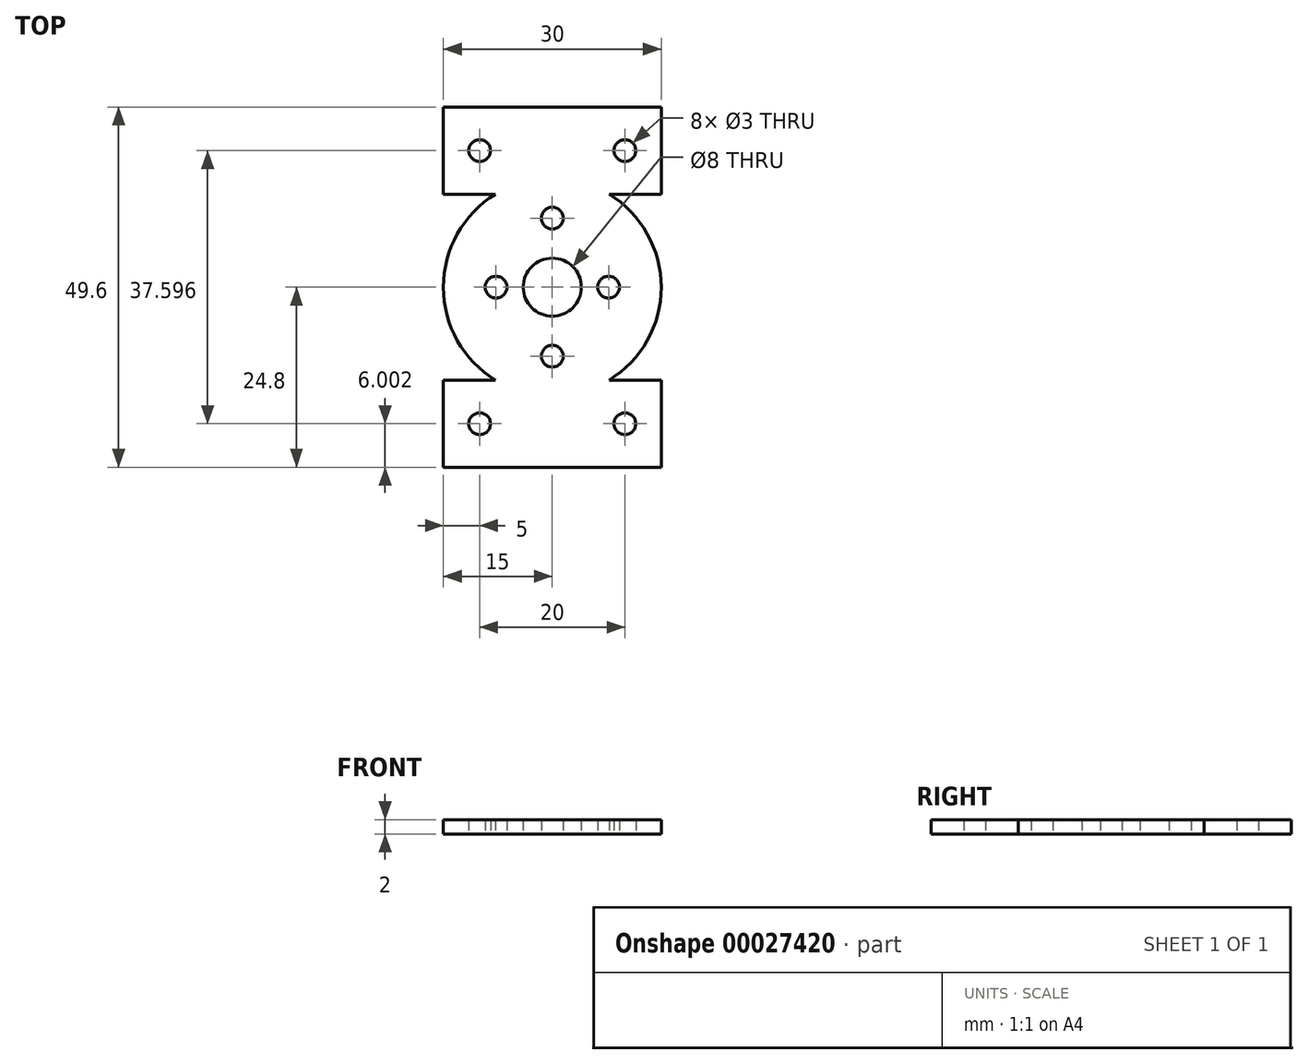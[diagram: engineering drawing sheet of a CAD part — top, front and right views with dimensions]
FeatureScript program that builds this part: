
annotation { "Feature Type Name" : "Feature", "Feature Type Description" : "" }
export const myFeature = defineFeature(function(context is Context, id is Id, definition is map)
    precondition{}
    {
        {
            var Q0;
            Q0=qCreatedBy(makeId("Top.planeOp"),FACE);
            var sketch = newSketch(context, id + "F0", { "sketchPlane" : qUnion([Q0])});
            skCircle(sketch, "E0", {"center": v(0, 9.5) * mm, "radius": 1.5 * mm});
            skCircle(sketch, "E1", {"center": v(-7.75, 0) * mm, "radius": 1.5 * mm});
            skCircle(sketch, "E2", {"center": v(0, 0) * mm, "radius": 4 * mm});
            skCircle(sketch, "E3", {"center": v(0, 0) * mm, "radius": 15 * mm});
            skLineSegment(sketch, "E4.rect.bottom", {"start": v(15, 12.8) * mm, "end": v(7.82, 12.8) * mm});
            skLineSegment(sketch, "E4.rect.top", {"start": v(15, 24.8) * mm, "end": v(-15, 24.8) * mm});
            skLineSegment(sketch, "E4.rect.left", {"start": v(15, 12.8) * mm, "end": v(15, 24.8) * mm});
            skLineSegment(sketch, "E4.rect.right", {"start": v(-15, 12.8) * mm, "end": v(-15, 24.8) * mm});
            skPoint(sketch, "E4.rect.middle", {"position": v(0, 18.8) * mm});
            skLineSegment(sketch, "E5.MirrorCS", {"start": v(15, -12.8) * mm, "end": v(7.82, -12.8) * mm});
            skLineSegment(sketch, "E6.MirrorCS", {"start": v(15, -24.8) * mm, "end": v(-15, -24.8) * mm});
            skLineSegment(sketch, "E7.MirrorCS", {"start": v(-15, -12.8) * mm, "end": v(-15, -24.8) * mm});
            skLineSegment(sketch, "E8.MirrorCS", {"start": v(15, -12.8) * mm, "end": v(15, -24.8) * mm});
            skPoint(sketch, "E9.MirrorP", {"position": v(0, -18.8) * mm});
            skLineSegment(sketch, "E10.trimOffspring", {"start": v(-7.82, 12.8) * mm, "end": v(-15, 12.8) * mm});
            skLineSegment(sketch, "E11.trimOffspring", {"start": v(-7.82, -12.8) * mm, "end": v(-15, -12.8) * mm});
            skCircle(sketch, "E12", {"center": v(-10, 18.8) * mm, "radius": 1.5 * mm});
            skCircle(sketch, "E13.MirrorC", {"center": v(10, 18.8) * mm, "radius": 1.5 * mm});
            skCircle(sketch, "E14.MirrorC", {"center": v(10, -18.8) * mm, "radius": 1.5 * mm});
            skCircle(sketch, "E15.MirrorC", {"center": v(-10, -18.8) * mm, "radius": 1.5 * mm});
            skCircle(sketch, "E16.MirrorC", {"center": v(0, -9.5) * mm, "radius": 1.5 * mm});
            skCircle(sketch, "E17.MirrorC", {"center": v(7.75, 0) * mm, "radius": 1.5 * mm});
            skSolve(sketch);
        }
        {
            var Q0;
            {var subQ1=sQuery(id+"F0.wireOp",EDGE,"E4.rect.bottom");Q0=makeQuery(id+"F0.imprint","IMPRINT",FACE,{"disambiguationData":[TD([[makeQuery(id+"F0.imprint","IMPRINT",EDGE,{"derivedFrom":subQ1}),-1.0]])]});}
            var Q1;
            Q1=makeQuery(id+"F0.imprint","IMPRINT",FACE,{"disambiguationData":[TD([[makeQuery(id+"F0.imprint","IMPRINT",EDGE,{"derivedFrom":sQuery(id+"F0.wireOp",EDGE,"E0")}),-1.0]])]});
            var Q2;
            {var subQ1=sQuery(id+"F0.wireOp",EDGE,"E5.MirrorCS");Q2=makeQuery(id+"F0.imprint","IMPRINT",FACE,{"disambiguationData":[TD([[makeQuery(id+"F0.imprint","IMPRINT",EDGE,{"derivedFrom":subQ1}),1.0]])]});}
            extrude(context, id + "F1", {"entities" : qUnion([Q0, Q1, Q2]), "depth" : 2 * mm});
        }
    });
